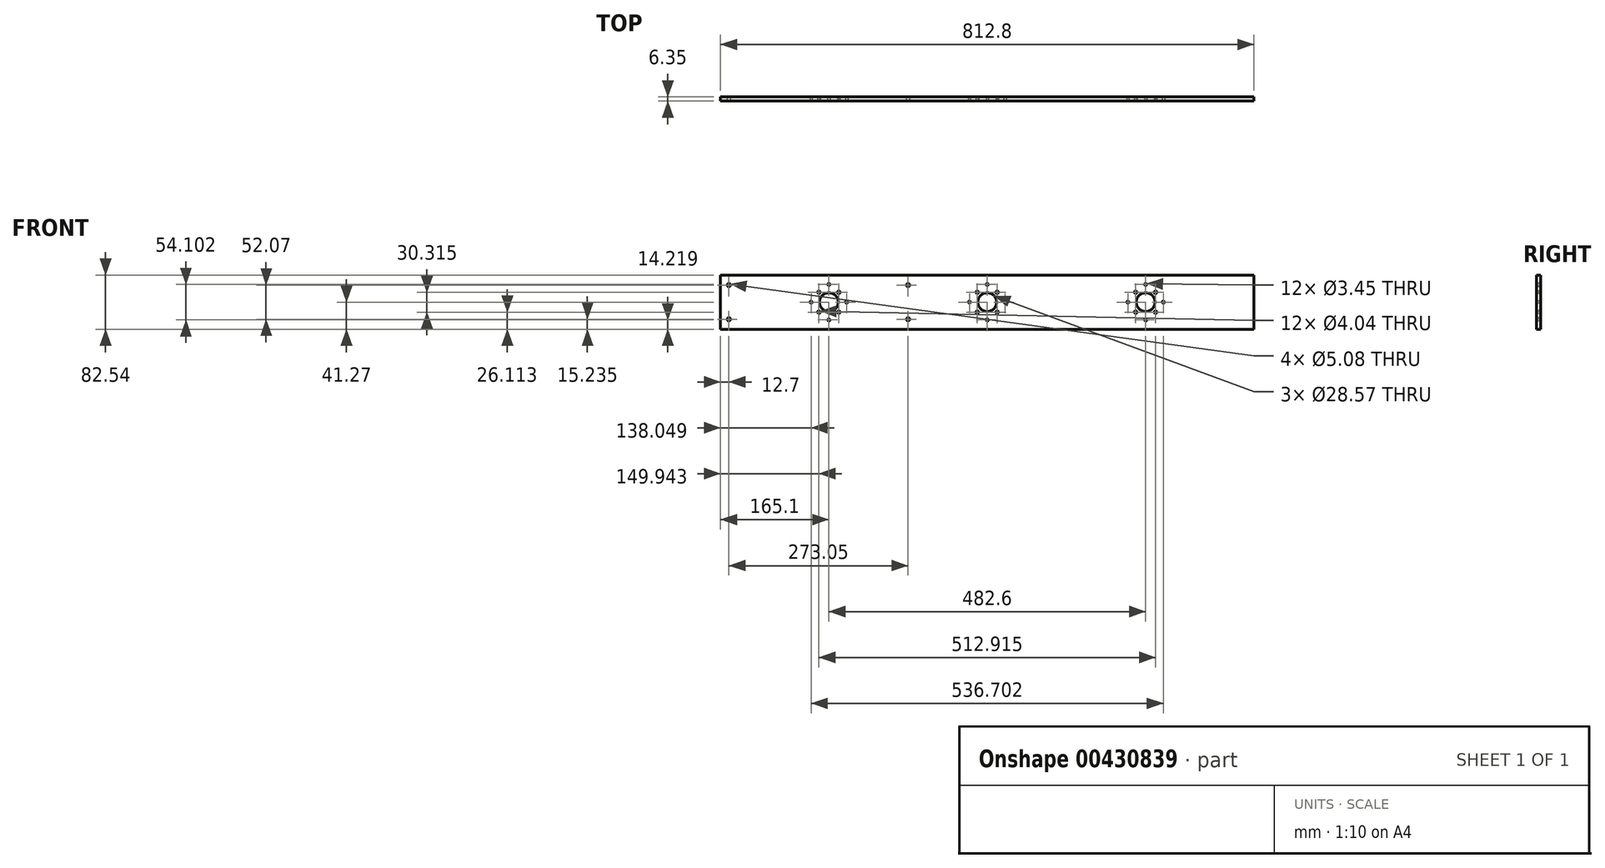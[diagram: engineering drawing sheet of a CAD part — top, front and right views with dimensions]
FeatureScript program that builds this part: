
annotation { "Feature Type Name" : "Feature", "Feature Type Description" : "" }
export const myFeature = defineFeature(function(context is Context, id is Id, definition is map)
    precondition{}
    {
        {
            var Q0;
            Q0=qCreatedBy(makeId("Front.planeOp"),FACE);
            var sketch = newSketch(context, id + "F0", { "sketchPlane" : qUnion([Q0])});
            skLineSegment(sketch, "E0.bottom", {"start": v(406.4, 41.28) * mm, "end": v(-406.4, 41.28) * mm});
            skLineSegment(sketch, "E0.top", {"start": v(406.4, -41.28) * mm, "end": v(-406.4, -41.28) * mm});
            skLineSegment(sketch, "E0.left", {"start": v(406.4, 41.28) * mm, "end": v(406.4, -41.28) * mm});
            skLineSegment(sketch, "E0.right", {"start": v(-406.4, 41.28) * mm, "end": v(-406.4, -41.28) * mm});
            skPoint(sketch, "E0.middle", {"position": v(0, 0) * mm});
            skSolve(sketch);
        }
        {
            var Q0;
            Q0=makeQuery(id+"F0.imprint","IMPRINT",FACE,{"disambiguationData":[TD([[makeQuery(id+"F0.imprint","IMPRINT",EDGE,{"derivedFrom":sQuery(id+"F0.wireOp",EDGE,"E0.bottom")}),1.0]])]});
            extrude(context, id + "F1", {"entities" : qUnion([Q0]), "depth" : 6.35 * mm});
        }
        {
            var Q0;
            Q0=makeQuery(id+"F1.opExtrude","CAP_FACE",FACE,{"disambiguationData":[OSD([sQuery(id+"F0.wireOp",EDGE,"E0.bottom"),sQuery(id+"F0.wireOp",EDGE,"E0.top"),sQuery(id+"F0.wireOp",EDGE,"E0.left"),sQuery(id+"F0.wireOp",EDGE,"E0.right")])],"isStart":false});
            var sketch = newSketch(context, id + "F2", { "sketchPlane" : qUnion([Q0])});
            skLineSegment(sketch, "E1", {"start": v(-406.4, 0) * mm, "end": v(-241.3, 0) * mm});
            skLineSegment(sketch, "E2", {"start": v(-241.3, 0) * mm, "end": v(-214.25, 0) * mm});
            skLineSegment(sketch, "E3", {"start": v(-241.3, 0) * mm, "end": v(-241.3, 27.05) * mm});
            skLineSegment(sketch, "E4", {"start": v(-241.3, 0) * mm, "end": v(-241.3, -27.05) * mm});
            skPoint(sketch, "E5", {"position": v(-268.35, 0) * mm});
            skCircle(sketch, "E6", {"center": v(-241.3, 27.05) * mm, "radius": 1.73 * mm});
            skCircle(sketch, "E7", {"center": v(-214.25, 0) * mm, "radius": 1.73 * mm});
            skCircle(sketch, "E8", {"center": v(-241.3, -27.05) * mm, "radius": 1.73 * mm});
            skCircle(sketch, "E9", {"center": v(-268.35, 0) * mm, "radius": 1.73 * mm});
            skCircle(sketch, "E10", {"center": v(-241.3, 0) * mm, "radius": 14.29 * mm});
            skLineSegment(sketch, "E11", {"start": v(406.4, 0) * mm, "end": v(241.3, 0) * mm});
            skPoint(sketch, "E11.endSnap0", {"position": v(406.4, 0) * mm});
            skPoint(sketch, "E12", {"position": v(268.35, 0) * mm});
            skLineSegment(sketch, "E13", {"start": v(241.3, 0) * mm, "end": v(241.3, 27.05) * mm});
            skLineSegment(sketch, "E14", {"start": v(241.3, 0) * mm, "end": v(241.3, -27.05) * mm});
            skLineSegment(sketch, "E15", {"start": v(241.3, 0) * mm, "end": v(214.25, 0) * mm});
            skCircle(sketch, "E16", {"center": v(241.3, 27.05) * mm, "radius": 1.73 * mm});
            skCircle(sketch, "E17", {"center": v(268.35, 0) * mm, "radius": 1.73 * mm});
            skCircle(sketch, "E18", {"center": v(241.3, -27.05) * mm, "radius": 1.73 * mm});
            skCircle(sketch, "E19", {"center": v(214.25, 0) * mm, "radius": 1.73 * mm});
            skCircle(sketch, "E20", {"center": v(241.3, 0) * mm, "radius": 14.29 * mm});
            skLineSegment(sketch, "E21", {"start": v(0, 0) * mm, "end": v(27.05, 0) * mm});
            skLineSegment(sketch, "E22", {"start": v(0, 0) * mm, "end": v(0, 27.05) * mm});
            skLineSegment(sketch, "E23", {"start": v(0, 0) * mm, "end": v(0, -27.05) * mm});
            skPoint(sketch, "E24", {"position": v(-27.05, 0.16) * mm});
            skCircle(sketch, "E25", {"center": v(0, 27.05) * mm, "radius": 1.73 * mm});
            skCircle(sketch, "E26", {"center": v(27.05, 0) * mm, "radius": 1.73 * mm});
            skCircle(sketch, "E27", {"center": v(0, -27.05) * mm, "radius": 1.73 * mm});
            skCircle(sketch, "E28", {"center": v(-27.05, 0.16) * mm, "radius": 1.73 * mm});
            skCircle(sketch, "E29", {"center": v(0, 0) * mm, "radius": 14.29 * mm});
            skLineSegment(sketch, "E30", {"start": v(241.3, 15.16) * mm, "end": v(256.46, 15.16) * mm});
            skLineSegment(sketch, "E31", {"start": v(256.46, 15.16) * mm, "end": v(256.46, -15.16) * mm});
            skLineSegment(sketch, "E32", {"start": v(256.46, -15.16) * mm, "end": v(226.14, -15.16) * mm});
            skLineSegment(sketch, "E33", {"start": v(226.14, -15.16) * mm, "end": v(226.14, 15.16) * mm});
            skLineSegment(sketch, "E34", {"start": v(226.14, 15.16) * mm, "end": v(256.46, 15.16) * mm});
            skCircle(sketch, "E35", {"center": v(226.14, 15.16) * mm, "radius": 2.02 * mm});
            skCircle(sketch, "E36", {"center": v(256.46, 15.16) * mm, "radius": 2.02 * mm});
            skCircle(sketch, "E37", {"center": v(256.46, -15.16) * mm, "radius": 2.02 * mm});
            skCircle(sketch, "E38", {"center": v(226.14, -15.16) * mm, "radius": 2.02 * mm});
            skLineSegment(sketch, "E39", {"start": v(15.16, 15.16) * mm, "end": v(15.16, -15.16) * mm});
            skLineSegment(sketch, "E40", {"start": v(15.16, -15.16) * mm, "end": v(-15.16, -15.16) * mm});
            skLineSegment(sketch, "E41", {"start": v(-15.16, -15.16) * mm, "end": v(-15.16, 15.16) * mm});
            skLineSegment(sketch, "E42", {"start": v(-15.16, 15.16) * mm, "end": v(15.16, 15.16) * mm});
            skCircle(sketch, "E43", {"center": v(-15.16, 15.16) * mm, "radius": 2.02 * mm});
            skCircle(sketch, "E44", {"center": v(15.16, 15.16) * mm, "radius": 2.02 * mm});
            skCircle(sketch, "E45", {"center": v(15.16, -15.16) * mm, "radius": 2.02 * mm});
            skCircle(sketch, "E46", {"center": v(-15.16, -15.16) * mm, "radius": 2.02 * mm});
            skLineSegment(sketch, "E47", {"start": v(15.16, 0) * mm, "end": v(-15.16, 0) * mm});
            skLineSegment(sketch, "E48", {"start": v(-226.14, 15.16) * mm, "end": v(-226.14, -15.16) * mm});
            skLineSegment(sketch, "E49", {"start": v(-226.14, -15.16) * mm, "end": v(-256.46, -15.16) * mm});
            skLineSegment(sketch, "E50", {"start": v(-256.46, -15.16) * mm, "end": v(-256.46, 15.16) * mm});
            skLineSegment(sketch, "E51", {"start": v(-256.46, 15.16) * mm, "end": v(-226.14, 15.16) * mm});
            skCircle(sketch, "E52", {"center": v(-256.46, 15.16) * mm, "radius": 2.02 * mm});
            skCircle(sketch, "E53", {"center": v(-226.14, 15.16) * mm, "radius": 2.02 * mm});
            skCircle(sketch, "E54", {"center": v(-226.14, -15.16) * mm, "radius": 2.02 * mm});
            skCircle(sketch, "E55", {"center": v(-256.46, -15.16) * mm, "radius": 2.02 * mm});
            skLineSegment(sketch, "E56", {"start": v(-256.46, 0) * mm, "end": v(-226.14, 0) * mm});
            skLineSegment(sketch, "E57", {"start": v(0, 41.28) * mm, "end": v(-38.1, 41.28) * mm});
            skLineSegment(sketch, "E58", {"start": v(-38.1, 41.28) * mm, "end": v(-38.1, -41.28) * mm});
            skPoint(sketch, "E59", {"position": v(-38.1, 0) * mm});
            skSolve(sketch);
        }
        {
            var Q0;
            {var subQ1=sQuery(id+"F2.wireOp",EDGE,"E4");var subQ3=sQuery(id+"F2.wireOp",EDGE,"E10");var subQ4=makeQuery(id+"F2.imprint","INTERSECT",VERTEX,{"derivedFrom":[subQ1,subQ3]});Q0=makeQuery(id+"F2.imprint","IMPRINT",FACE,{"disambiguationData":[TD([[makeQuery(id+"F2.imprint","IMPRINT",EDGE,{"disambiguationData":[TD([[subQ4,-1.0]])],"derivedFrom":subQ3}),1.0]])]});}
            var Q1;
            {var subQ1=sQuery(id+"F2.wireOp",EDGE,"E3");var subQ3=sQuery(id+"F2.wireOp",EDGE,"E10");var subQ4=makeQuery(id+"F2.imprint","INTERSECT",VERTEX,{"derivedFrom":[subQ1,subQ3]});Q1=makeQuery(id+"F2.imprint","IMPRINT",FACE,{"disambiguationData":[TD([[makeQuery(id+"F2.imprint","IMPRINT",EDGE,{"disambiguationData":[TD([[subQ4,1.0]])],"derivedFrom":subQ3}),1.0]])]});}
            var Q2;
            {var subQ1=sQuery(id+"F2.wireOp",EDGE,"E3");var subQ3=sQuery(id+"F2.wireOp",EDGE,"E10");var subQ4=makeQuery(id+"F2.imprint","INTERSECT",VERTEX,{"derivedFrom":[subQ1,subQ3]});Q2=makeQuery(id+"F2.imprint","IMPRINT",FACE,{"disambiguationData":[TD([[makeQuery(id+"F2.imprint","IMPRINT",EDGE,{"disambiguationData":[TD([[subQ4,-1.0]])],"derivedFrom":subQ3}),1.0]])]});}
            var Q3;
            {var subQ1=sQuery(id+"F2.wireOp",EDGE,"E4");var subQ3=sQuery(id+"F2.wireOp",EDGE,"E10");var subQ4=makeQuery(id+"F2.imprint","INTERSECT",VERTEX,{"derivedFrom":[subQ1,subQ3]});Q3=makeQuery(id+"F2.imprint","IMPRINT",FACE,{"disambiguationData":[TD([[makeQuery(id+"F2.imprint","IMPRINT",EDGE,{"disambiguationData":[TD([[subQ4,1.0]])],"derivedFrom":subQ3}),1.0]])]});}
            var Q4;
            {var subQ0=sQuery(id+"F2.wireOp",EDGE,"E50");var subQ1=sQuery(id+"F2.wireOp",EDGE,"E49");var subQ2=makeQuery(id+"F2.imprint","INTERSECT",VERTEX,{"derivedFrom":[subQ1,subQ0]});Q4=makeQuery(id+"F2.imprint","IMPRINT",FACE,{"disambiguationData":[TD([[makeQuery(id+"F2.imprint","IMPRINT",EDGE,{"disambiguationData":[TD([[subQ2,1.0]])],"derivedFrom":subQ1}),1.0]])]});}
            var Q5;
            {var subQ0=sQuery(id+"F2.wireOp",EDGE,"E50");var subQ1=sQuery(id+"F2.wireOp",EDGE,"E49");var subQ2=makeQuery(id+"F2.imprint","INTERSECT",VERTEX,{"derivedFrom":[subQ1,subQ0]});Q5=makeQuery(id+"F2.imprint","IMPRINT",FACE,{"disambiguationData":[TD([[makeQuery(id+"F2.imprint","IMPRINT",EDGE,{"disambiguationData":[TD([[subQ2,1.0]])],"derivedFrom":subQ1}),-1.0]])]});}
            var Q6;
            Q6=makeQuery(id+"F2.imprint","IMPRINT",FACE,{"disambiguationData":[TD([[makeQuery(id+"F2.imprint","IMPRINT",EDGE,{"derivedFrom":sQuery(id+"F2.wireOp",EDGE,"E8")}),1.0]])]});
            var Q7;
            {var subQ0=sQuery(id+"F2.wireOp",EDGE,"E49");var subQ1=sQuery(id+"F2.wireOp",EDGE,"E48");var subQ2=makeQuery(id+"F2.imprint","INTERSECT",VERTEX,{"derivedFrom":[subQ1,subQ0]});Q7=makeQuery(id+"F2.imprint","IMPRINT",FACE,{"disambiguationData":[TD([[makeQuery(id+"F2.imprint","IMPRINT",EDGE,{"disambiguationData":[TD([[subQ2,1.0]])],"derivedFrom":subQ1}),1.0]])]});}
            var Q8;
            {var subQ0=sQuery(id+"F2.wireOp",EDGE,"E49");var subQ1=sQuery(id+"F2.wireOp",EDGE,"E48");var subQ2=makeQuery(id+"F2.imprint","INTERSECT",VERTEX,{"derivedFrom":[subQ1,subQ0]});Q8=makeQuery(id+"F2.imprint","IMPRINT",FACE,{"disambiguationData":[TD([[makeQuery(id+"F2.imprint","IMPRINT",EDGE,{"disambiguationData":[TD([[subQ2,1.0]])],"derivedFrom":subQ1}),-1.0]])]});}
            var Q9;
            {var subQ0=sQuery(id+"F2.wireOp",EDGE,"E51");var subQ1=sQuery(id+"F2.wireOp",EDGE,"E48");var subQ2=makeQuery(id+"F2.imprint","INTERSECT",VERTEX,{"derivedFrom":[subQ1,subQ0]});Q9=makeQuery(id+"F2.imprint","IMPRINT",FACE,{"disambiguationData":[TD([[makeQuery(id+"F2.imprint","IMPRINT",EDGE,{"disambiguationData":[TD([[subQ2,-1.0]])],"derivedFrom":subQ1}),1.0]])]});}
            var Q10;
            {var subQ0=sQuery(id+"F2.wireOp",EDGE,"E51");var subQ1=sQuery(id+"F2.wireOp",EDGE,"E48");var subQ2=makeQuery(id+"F2.imprint","INTERSECT",VERTEX,{"derivedFrom":[subQ1,subQ0]});Q10=makeQuery(id+"F2.imprint","IMPRINT",FACE,{"disambiguationData":[TD([[makeQuery(id+"F2.imprint","IMPRINT",EDGE,{"disambiguationData":[TD([[subQ2,-1.0]])],"derivedFrom":subQ1}),-1.0]])]});}
            var Q11;
            Q11=makeQuery(id+"F2.imprint","IMPRINT",FACE,{"disambiguationData":[TD([[makeQuery(id+"F2.imprint","IMPRINT",EDGE,{"derivedFrom":sQuery(id+"F2.wireOp",EDGE,"E7")}),1.0]])]});
            var Q12;
            Q12=makeQuery(id+"F2.imprint","IMPRINT",FACE,{"disambiguationData":[TD([[makeQuery(id+"F2.imprint","IMPRINT",EDGE,{"derivedFrom":sQuery(id+"F2.wireOp",EDGE,"E6")}),1.0]])]});
            var Q13;
            {var subQ0=sQuery(id+"F2.wireOp",EDGE,"E51");var subQ1=sQuery(id+"F2.wireOp",EDGE,"E50");var subQ2=makeQuery(id+"F2.imprint","INTERSECT",VERTEX,{"derivedFrom":[subQ1,subQ0]});Q13=makeQuery(id+"F2.imprint","IMPRINT",FACE,{"disambiguationData":[TD([[makeQuery(id+"F2.imprint","IMPRINT",EDGE,{"disambiguationData":[TD([[subQ2,1.0]])],"derivedFrom":subQ1}),-1.0]])]});}
            var Q14;
            {var subQ0=sQuery(id+"F2.wireOp",EDGE,"E51");var subQ1=sQuery(id+"F2.wireOp",EDGE,"E50");var subQ2=makeQuery(id+"F2.imprint","INTERSECT",VERTEX,{"derivedFrom":[subQ1,subQ0]});Q14=makeQuery(id+"F2.imprint","IMPRINT",FACE,{"disambiguationData":[TD([[makeQuery(id+"F2.imprint","IMPRINT",EDGE,{"disambiguationData":[TD([[subQ2,1.0]])],"derivedFrom":subQ1}),1.0]])]});}
            var Q15;
            {var subQ0=sQuery(id+"F2.wireOp",EDGE,"E9");var subQ1=sQuery(id+"F2.wireOp",EDGE,"E1");var subQ2=makeQuery(id+"F2.imprint","INTERSECT",VERTEX,{"disambiguationData":[OD(0.0)],"derivedFrom":[subQ1,subQ0]});Q15=makeQuery(id+"F2.imprint","IMPRINT",FACE,{"disambiguationData":[TD([[makeQuery(id+"F2.imprint","IMPRINT",EDGE,{"disambiguationData":[TD([[subQ2,-1.0]])],"derivedFrom":subQ1}),-1.0]])]});}
            var Q16;
            {var subQ0=sQuery(id+"F2.wireOp",EDGE,"E9");var subQ1=sQuery(id+"F2.wireOp",EDGE,"E1");var subQ2=makeQuery(id+"F2.imprint","INTERSECT",VERTEX,{"disambiguationData":[OD(0.0)],"derivedFrom":[subQ1,subQ0]});Q16=makeQuery(id+"F2.imprint","IMPRINT",FACE,{"disambiguationData":[TD([[makeQuery(id+"F2.imprint","IMPRINT",EDGE,{"disambiguationData":[TD([[subQ2,-1.0]])],"derivedFrom":subQ1}),1.0]])]});}
            var Q17;
            {var subQ1=sQuery(id+"F2.wireOp",EDGE,"E23");var subQ3=sQuery(id+"F2.wireOp",EDGE,"E29");var subQ4=makeQuery(id+"F2.imprint","INTERSECT",VERTEX,{"derivedFrom":[subQ1,subQ3]});Q17=makeQuery(id+"F2.imprint","IMPRINT",FACE,{"disambiguationData":[TD([[makeQuery(id+"F2.imprint","IMPRINT",EDGE,{"disambiguationData":[TD([[subQ4,-1.0]])],"derivedFrom":subQ3}),1.0]])]});}
            var Q18;
            {var subQ1=sQuery(id+"F2.wireOp",EDGE,"E23");var subQ3=sQuery(id+"F2.wireOp",EDGE,"E29");var subQ4=makeQuery(id+"F2.imprint","INTERSECT",VERTEX,{"derivedFrom":[subQ1,subQ3]});Q18=makeQuery(id+"F2.imprint","IMPRINT",FACE,{"disambiguationData":[TD([[makeQuery(id+"F2.imprint","IMPRINT",EDGE,{"disambiguationData":[TD([[subQ4,1.0]])],"derivedFrom":subQ3}),1.0]])]});}
            var Q19;
            {var subQ1=sQuery(id+"F2.wireOp",EDGE,"E22");var subQ3=sQuery(id+"F2.wireOp",EDGE,"E29");var subQ4=makeQuery(id+"F2.imprint","INTERSECT",VERTEX,{"derivedFrom":[subQ1,subQ3]});Q19=makeQuery(id+"F2.imprint","IMPRINT",FACE,{"disambiguationData":[TD([[makeQuery(id+"F2.imprint","IMPRINT",EDGE,{"disambiguationData":[TD([[subQ4,-1.0]])],"derivedFrom":subQ3}),1.0]])]});}
            var Q20;
            {var subQ1=sQuery(id+"F2.wireOp",EDGE,"E22");var subQ3=sQuery(id+"F2.wireOp",EDGE,"E29");var subQ4=makeQuery(id+"F2.imprint","INTERSECT",VERTEX,{"derivedFrom":[subQ1,subQ3]});Q20=makeQuery(id+"F2.imprint","IMPRINT",FACE,{"disambiguationData":[TD([[makeQuery(id+"F2.imprint","IMPRINT",EDGE,{"disambiguationData":[TD([[subQ4,1.0]])],"derivedFrom":subQ3}),1.0]])]});}
            var Q21;
            {var subQ0=sQuery(id+"F2.wireOp",EDGE,"E42");var subQ1=sQuery(id+"F2.wireOp",EDGE,"E39");var subQ2=makeQuery(id+"F2.imprint","INTERSECT",VERTEX,{"derivedFrom":[subQ1,subQ0]});Q21=makeQuery(id+"F2.imprint","IMPRINT",FACE,{"disambiguationData":[TD([[makeQuery(id+"F2.imprint","IMPRINT",EDGE,{"disambiguationData":[TD([[subQ2,-1.0]])],"derivedFrom":subQ1}),1.0]])]});}
            var Q22;
            {var subQ0=sQuery(id+"F2.wireOp",EDGE,"E42");var subQ1=sQuery(id+"F2.wireOp",EDGE,"E39");var subQ2=makeQuery(id+"F2.imprint","INTERSECT",VERTEX,{"derivedFrom":[subQ1,subQ0]});Q22=makeQuery(id+"F2.imprint","IMPRINT",FACE,{"disambiguationData":[TD([[makeQuery(id+"F2.imprint","IMPRINT",EDGE,{"disambiguationData":[TD([[subQ2,-1.0]])],"derivedFrom":subQ1}),-1.0]])]});}
            var Q23;
            Q23=makeQuery(id+"F2.imprint","IMPRINT",FACE,{"disambiguationData":[TD([[makeQuery(id+"F2.imprint","IMPRINT",EDGE,{"derivedFrom":sQuery(id+"F2.wireOp",EDGE,"E25")}),1.0]])]});
            var Q24;
            {var subQ0=sQuery(id+"F2.wireOp",EDGE,"E42");var subQ1=sQuery(id+"F2.wireOp",EDGE,"E41");var subQ2=makeQuery(id+"F2.imprint","INTERSECT",VERTEX,{"derivedFrom":[subQ1,subQ0]});Q24=makeQuery(id+"F2.imprint","IMPRINT",FACE,{"disambiguationData":[TD([[makeQuery(id+"F2.imprint","IMPRINT",EDGE,{"disambiguationData":[TD([[subQ2,1.0]])],"derivedFrom":subQ1}),1.0]])]});}
            var Q25;
            {var subQ0=sQuery(id+"F2.wireOp",EDGE,"E42");var subQ1=sQuery(id+"F2.wireOp",EDGE,"E41");var subQ2=makeQuery(id+"F2.imprint","INTERSECT",VERTEX,{"derivedFrom":[subQ1,subQ0]});Q25=makeQuery(id+"F2.imprint","IMPRINT",FACE,{"disambiguationData":[TD([[makeQuery(id+"F2.imprint","IMPRINT",EDGE,{"disambiguationData":[TD([[subQ2,1.0]])],"derivedFrom":subQ1}),-1.0]])]});}
            var Q26;
            {var subQ0=sQuery(id+"F2.wireOp",EDGE,"E41");var subQ1=sQuery(id+"F2.wireOp",EDGE,"E40");var subQ2=makeQuery(id+"F2.imprint","INTERSECT",VERTEX,{"derivedFrom":[subQ1,subQ0]});Q26=makeQuery(id+"F2.imprint","IMPRINT",FACE,{"disambiguationData":[TD([[makeQuery(id+"F2.imprint","IMPRINT",EDGE,{"disambiguationData":[TD([[subQ2,1.0]])],"derivedFrom":subQ1}),1.0]])]});}
            var Q27;
            {var subQ0=sQuery(id+"F2.wireOp",EDGE,"E41");var subQ1=sQuery(id+"F2.wireOp",EDGE,"E40");var subQ2=makeQuery(id+"F2.imprint","INTERSECT",VERTEX,{"derivedFrom":[subQ1,subQ0]});Q27=makeQuery(id+"F2.imprint","IMPRINT",FACE,{"disambiguationData":[TD([[makeQuery(id+"F2.imprint","IMPRINT",EDGE,{"disambiguationData":[TD([[subQ2,1.0]])],"derivedFrom":subQ1}),-1.0]])]});}
            var Q28;
            Q28=makeQuery(id+"F2.imprint","IMPRINT",FACE,{"disambiguationData":[TD([[makeQuery(id+"F2.imprint","IMPRINT",EDGE,{"derivedFrom":sQuery(id+"F2.wireOp",EDGE,"E27")}),1.0]])]});
            var Q29;
            {var subQ0=sQuery(id+"F2.wireOp",EDGE,"E40");var subQ1=sQuery(id+"F2.wireOp",EDGE,"E39");var subQ2=makeQuery(id+"F2.imprint","INTERSECT",VERTEX,{"derivedFrom":[subQ1,subQ0]});Q29=makeQuery(id+"F2.imprint","IMPRINT",FACE,{"disambiguationData":[TD([[makeQuery(id+"F2.imprint","IMPRINT",EDGE,{"disambiguationData":[TD([[subQ2,1.0]])],"derivedFrom":subQ1}),1.0]])]});}
            var Q30;
            {var subQ0=sQuery(id+"F2.wireOp",EDGE,"E40");var subQ1=sQuery(id+"F2.wireOp",EDGE,"E39");var subQ2=makeQuery(id+"F2.imprint","INTERSECT",VERTEX,{"derivedFrom":[subQ1,subQ0]});Q30=makeQuery(id+"F2.imprint","IMPRINT",FACE,{"disambiguationData":[TD([[makeQuery(id+"F2.imprint","IMPRINT",EDGE,{"disambiguationData":[TD([[subQ2,1.0]])],"derivedFrom":subQ1}),-1.0]])]});}
            var Q31;
            Q31=makeQuery(id+"F2.imprint","IMPRINT",FACE,{"disambiguationData":[TD([[makeQuery(id+"F2.imprint","IMPRINT",EDGE,{"derivedFrom":sQuery(id+"F2.wireOp",EDGE,"E28")}),1.0]])]});
            var Q32;
            Q32=makeQuery(id+"F2.imprint","IMPRINT",FACE,{"disambiguationData":[TD([[makeQuery(id+"F2.imprint","IMPRINT",EDGE,{"derivedFrom":sQuery(id+"F2.wireOp",EDGE,"E26")}),1.0]])]});
            var Q33;
            {var subQ1=sQuery(id+"F2.wireOp",EDGE,"E11");var subQ3=sQuery(id+"F2.wireOp",EDGE,"E20");var subQ4=makeQuery(id+"F2.imprint","INTERSECT",VERTEX,{"derivedFrom":[subQ1,subQ3]});Q33=makeQuery(id+"F2.imprint","IMPRINT",FACE,{"disambiguationData":[TD([[makeQuery(id+"F2.imprint","IMPRINT",EDGE,{"disambiguationData":[TD([[subQ4,1.0]])],"derivedFrom":subQ3}),1.0]])]});}
            var Q34;
            {var subQ1=sQuery(id+"F2.wireOp",EDGE,"E11");var subQ3=sQuery(id+"F2.wireOp",EDGE,"E20");var subQ4=makeQuery(id+"F2.imprint","INTERSECT",VERTEX,{"derivedFrom":[subQ1,subQ3]});Q34=makeQuery(id+"F2.imprint","IMPRINT",FACE,{"disambiguationData":[TD([[makeQuery(id+"F2.imprint","IMPRINT",EDGE,{"disambiguationData":[TD([[subQ4,-1.0]])],"derivedFrom":subQ3}),1.0]])]});}
            var Q35;
            {var subQ1=sQuery(id+"F2.wireOp",EDGE,"E13");var subQ3=sQuery(id+"F2.wireOp",EDGE,"E20");var subQ4=makeQuery(id+"F2.imprint","INTERSECT",VERTEX,{"derivedFrom":[subQ1,subQ3]});Q35=makeQuery(id+"F2.imprint","IMPRINT",FACE,{"disambiguationData":[TD([[makeQuery(id+"F2.imprint","IMPRINT",EDGE,{"disambiguationData":[TD([[subQ4,-1.0]])],"derivedFrom":subQ3}),1.0]])]});}
            var Q36;
            {var subQ1=sQuery(id+"F2.wireOp",EDGE,"E14");var subQ3=sQuery(id+"F2.wireOp",EDGE,"E20");var subQ4=makeQuery(id+"F2.imprint","INTERSECT",VERTEX,{"derivedFrom":[subQ1,subQ3]});Q36=makeQuery(id+"F2.imprint","IMPRINT",FACE,{"disambiguationData":[TD([[makeQuery(id+"F2.imprint","IMPRINT",EDGE,{"disambiguationData":[TD([[subQ4,1.0]])],"derivedFrom":subQ3}),1.0]])]});}
            var Q37;
            {var subQ0=sQuery(id+"F2.wireOp",EDGE,"E32");var subQ1=sQuery(id+"F2.wireOp",EDGE,"E31");var subQ2=makeQuery(id+"F2.imprint","INTERSECT",VERTEX,{"derivedFrom":[subQ1,subQ0]});Q37=makeQuery(id+"F2.imprint","IMPRINT",FACE,{"disambiguationData":[TD([[makeQuery(id+"F2.imprint","IMPRINT",EDGE,{"disambiguationData":[TD([[subQ2,1.0]])],"derivedFrom":subQ1}),1.0]])]});}
            var Q38;
            {var subQ0=sQuery(id+"F2.wireOp",EDGE,"E32");var subQ1=sQuery(id+"F2.wireOp",EDGE,"E31");var subQ2=makeQuery(id+"F2.imprint","INTERSECT",VERTEX,{"derivedFrom":[subQ1,subQ0]});Q38=makeQuery(id+"F2.imprint","IMPRINT",FACE,{"disambiguationData":[TD([[makeQuery(id+"F2.imprint","IMPRINT",EDGE,{"disambiguationData":[TD([[subQ2,1.0]])],"derivedFrom":subQ1}),-1.0]])]});}
            var Q39;
            Q39=makeQuery(id+"F2.imprint","IMPRINT",FACE,{"disambiguationData":[TD([[makeQuery(id+"F2.imprint","IMPRINT",EDGE,{"derivedFrom":sQuery(id+"F2.wireOp",EDGE,"E18")}),1.0]])]});
            var Q40;
            {var subQ0=sQuery(id+"F2.wireOp",EDGE,"E17");var subQ1=sQuery(id+"F2.wireOp",EDGE,"E11");var subQ2=makeQuery(id+"F2.imprint","INTERSECT",VERTEX,{"disambiguationData":[OD(0.0)],"derivedFrom":[subQ1,subQ0]});Q40=makeQuery(id+"F2.imprint","IMPRINT",FACE,{"disambiguationData":[TD([[makeQuery(id+"F2.imprint","IMPRINT",EDGE,{"disambiguationData":[TD([[subQ2,1.0]])],"derivedFrom":subQ1}),1.0]])]});}
            var Q41;
            {var subQ0=sQuery(id+"F2.wireOp",EDGE,"E17");var subQ1=sQuery(id+"F2.wireOp",EDGE,"E11");var subQ2=makeQuery(id+"F2.imprint","INTERSECT",VERTEX,{"disambiguationData":[OD(0.0)],"derivedFrom":[subQ1,subQ0]});Q41=makeQuery(id+"F2.imprint","IMPRINT",FACE,{"disambiguationData":[TD([[makeQuery(id+"F2.imprint","IMPRINT",EDGE,{"disambiguationData":[TD([[subQ2,1.0]])],"derivedFrom":subQ1}),-1.0]])]});}
            var Q42;
            {var subQ0=sQuery(id+"F2.wireOp",EDGE,"E34");var subQ1=sQuery(id+"F2.wireOp",EDGE,"E31");var subQ2=makeQuery(id+"F2.imprint","INTERSECT",VERTEX,{"derivedFrom":[subQ1,subQ0]});Q42=makeQuery(id+"F2.imprint","IMPRINT",FACE,{"disambiguationData":[TD([[makeQuery(id+"F2.imprint","IMPRINT",EDGE,{"disambiguationData":[TD([[subQ2,-1.0]])],"derivedFrom":subQ1}),1.0]])]});}
            var Q43;
            {var subQ0=sQuery(id+"F2.wireOp",EDGE,"E34");var subQ1=sQuery(id+"F2.wireOp",EDGE,"E31");var subQ2=makeQuery(id+"F2.imprint","INTERSECT",VERTEX,{"derivedFrom":[subQ1,subQ0]});Q43=makeQuery(id+"F2.imprint","IMPRINT",FACE,{"disambiguationData":[TD([[makeQuery(id+"F2.imprint","IMPRINT",EDGE,{"disambiguationData":[TD([[subQ2,-1.0]])],"derivedFrom":subQ1}),-1.0]])]});}
            var Q44;
            Q44=makeQuery(id+"F2.imprint","IMPRINT",FACE,{"disambiguationData":[TD([[makeQuery(id+"F2.imprint","IMPRINT",EDGE,{"derivedFrom":sQuery(id+"F2.wireOp",EDGE,"E16")}),1.0]])]});
            var Q45;
            {var subQ0=sQuery(id+"F2.wireOp",EDGE,"E34");var subQ1=sQuery(id+"F2.wireOp",EDGE,"E33");var subQ2=makeQuery(id+"F2.imprint","INTERSECT",VERTEX,{"derivedFrom":[subQ1,subQ0]});Q45=makeQuery(id+"F2.imprint","IMPRINT",FACE,{"disambiguationData":[TD([[makeQuery(id+"F2.imprint","IMPRINT",EDGE,{"disambiguationData":[TD([[subQ2,1.0]])],"derivedFrom":subQ1}),-1.0]])]});}
            var Q46;
            {var subQ0=sQuery(id+"F2.wireOp",EDGE,"E34");var subQ1=sQuery(id+"F2.wireOp",EDGE,"E33");var subQ2=makeQuery(id+"F2.imprint","INTERSECT",VERTEX,{"derivedFrom":[subQ1,subQ0]});Q46=makeQuery(id+"F2.imprint","IMPRINT",FACE,{"disambiguationData":[TD([[makeQuery(id+"F2.imprint","IMPRINT",EDGE,{"disambiguationData":[TD([[subQ2,1.0]])],"derivedFrom":subQ1}),1.0]])]});}
            var Q47;
            {var subQ0=sQuery(id+"F2.wireOp",EDGE,"E33");var subQ1=sQuery(id+"F2.wireOp",EDGE,"E32");var subQ2=makeQuery(id+"F2.imprint","INTERSECT",VERTEX,{"derivedFrom":[subQ1,subQ0]});Q47=makeQuery(id+"F2.imprint","IMPRINT",FACE,{"disambiguationData":[TD([[makeQuery(id+"F2.imprint","IMPRINT",EDGE,{"disambiguationData":[TD([[subQ2,1.0]])],"derivedFrom":subQ1}),1.0]])]});}
            var Q48;
            {var subQ0=sQuery(id+"F2.wireOp",EDGE,"E33");var subQ1=sQuery(id+"F2.wireOp",EDGE,"E32");var subQ2=makeQuery(id+"F2.imprint","INTERSECT",VERTEX,{"derivedFrom":[subQ1,subQ0]});Q48=makeQuery(id+"F2.imprint","IMPRINT",FACE,{"disambiguationData":[TD([[makeQuery(id+"F2.imprint","IMPRINT",EDGE,{"disambiguationData":[TD([[subQ2,1.0]])],"derivedFrom":subQ1}),-1.0]])]});}
            var Q49;
            Q49=makeQuery(id+"F2.imprint","IMPRINT",FACE,{"disambiguationData":[TD([[makeQuery(id+"F2.imprint","IMPRINT",EDGE,{"derivedFrom":sQuery(id+"F2.wireOp",EDGE,"E19")}),1.0]])]});
            var Q50;
            Q50=makeQuery(id+"F1.opExtrude","CAP_FACE",FACE,{"disambiguationData":[OSD([sQuery(id+"F0.wireOp",EDGE,"E0.bottom"),sQuery(id+"F0.wireOp",EDGE,"E0.top"),sQuery(id+"F0.wireOp",EDGE,"E0.left"),sQuery(id+"F0.wireOp",EDGE,"E0.right")])],"isStart":true});
            extrude(context, id + "F3", {"entities" : qUnion([Q0, Q1, Q2, Q3, Q4, Q5, Q6, Q7, Q8, Q9, Q10, Q11, Q12, Q13, Q14, Q15, Q16, Q17, Q18, Q19, Q20, Q21, Q22, Q23, Q24, Q25, Q26, Q27, Q28, Q29, Q30, Q31, Q32, Q33, Q34, Q35, Q36, Q37, Q38, Q39, Q40, Q41, Q42, Q43, Q44, Q45, Q46, Q47, Q48, Q49]), "operationType" : NewBodyOperationType.REMOVE, "endBound" : BoundingType.UP_TO_SURFACE, "oppositeDirection" : true, "endBoundEntityFace" : qUnion([Q50]), "depth" : 25.4 * mm});
        }
        {
            var Q0;
            Q0=makeQuery(id+"F1.opExtrude","CAP_FACE",FACE,{"disambiguationData":[OSD([sQuery(id+"F0.wireOp",EDGE,"E0.bottom"),sQuery(id+"F0.wireOp",EDGE,"E0.top"),sQuery(id+"F0.wireOp",EDGE,"E0.left"),sQuery(id+"F0.wireOp",EDGE,"E0.right")])],"isStart":false});
            var sketch = newSketch(context, id + "F4", { "sketchPlane" : qUnion([Q0])});
            skLineSegment(sketch, "E60", {"start": v(-393.7, 41.28) * mm, "end": v(-393.7, -41.28) * mm});
            skCircle(sketch, "E61", {"center": v(-393.7, -26.04) * mm, "radius": 2.54 * mm});
            skCircle(sketch, "E62", {"center": v(-393.7, 26.04) * mm, "radius": 2.54 * mm});
            skLineSegment(sketch, "E63", {"start": v(-241.3, 0) * mm, "end": v(-241.3, 41.27) * mm});
            skLineSegment(sketch, "E64", {"start": v(-241.3, 41.28) * mm, "end": v(0, 41.28) * mm});
            skLineSegment(sketch, "E65", {"start": v(-120.65, 41.28) * mm, "end": v(-120.65, -41.28) * mm});
            skCircle(sketch, "E66", {"center": v(-120.65, 26.04) * mm, "radius": 2.54 * mm});
            skCircle(sketch, "E67", {"center": v(-120.65, -26.04) * mm, "radius": 2.54 * mm});
            skSolve(sketch);
        }
        {
            var Q0;
            Q0 = qSketchRegion(id + "F4", true);
            var Q1;
            Q1=makeQuery(id+"F1.opExtrude","CAP_FACE",FACE,{"disambiguationData":[OSD([sQuery(id+"F0.wireOp",EDGE,"E0.bottom"),sQuery(id+"F0.wireOp",EDGE,"E0.top"),sQuery(id+"F0.wireOp",EDGE,"E0.left"),sQuery(id+"F0.wireOp",EDGE,"E0.right")])],"isStart":true});
            extrude(context, id + "F5", {"entities" : qUnion([Q0]), "operationType" : NewBodyOperationType.REMOVE, "endBound" : BoundingType.UP_TO_SURFACE, "oppositeDirection" : true, "endBoundEntityFace" : qUnion([Q1]), "depth" : 25.4 * mm});
        }
    });
